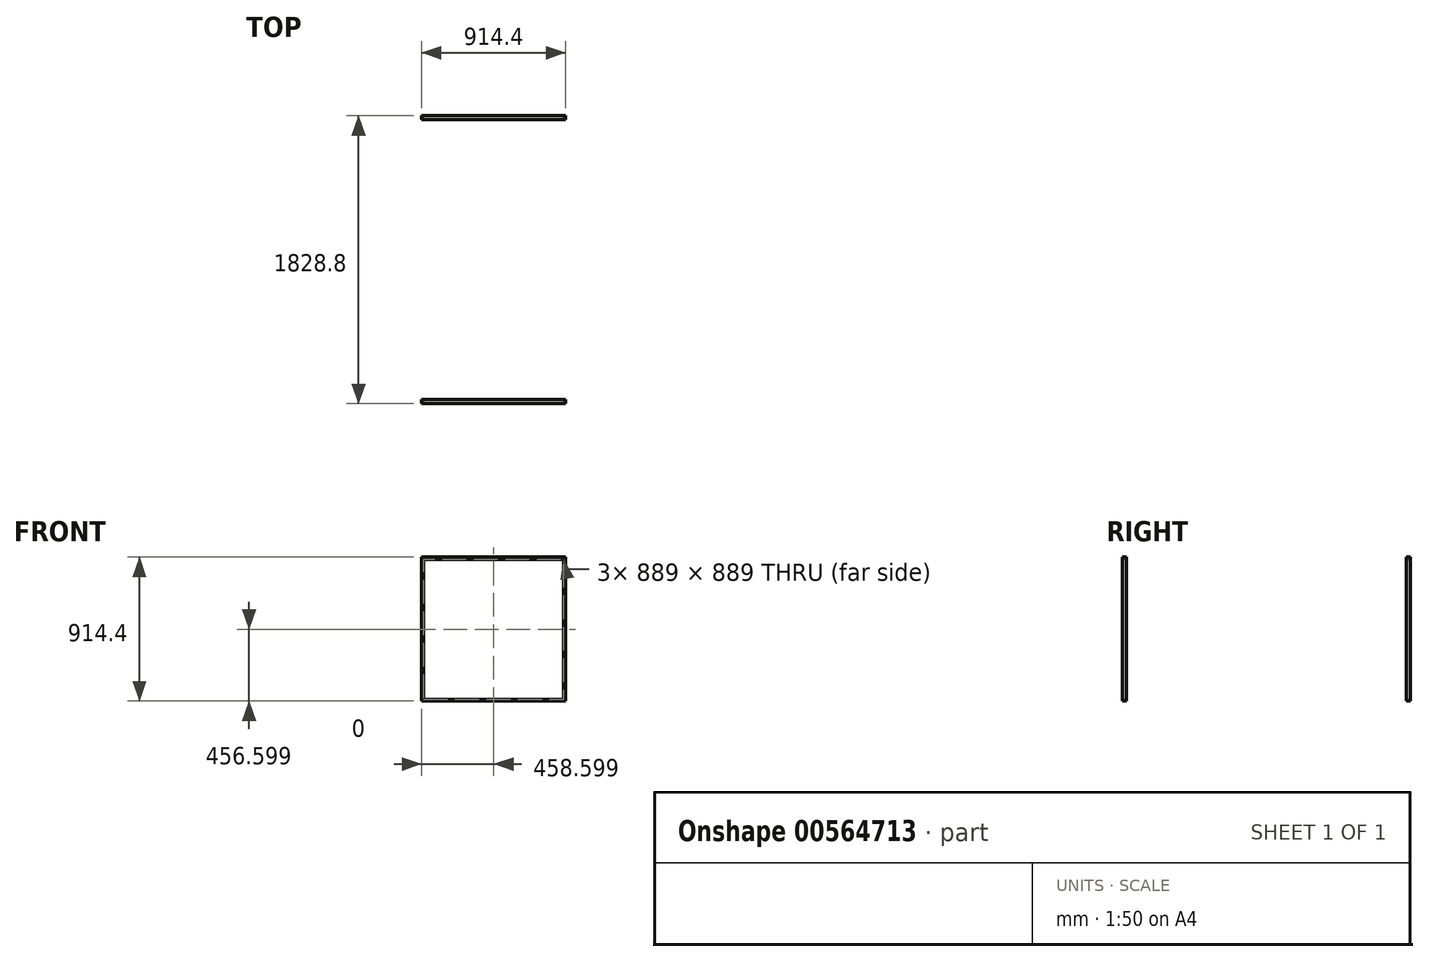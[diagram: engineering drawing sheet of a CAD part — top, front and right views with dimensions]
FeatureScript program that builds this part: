
annotation { "Feature Type Name" : "Feature", "Feature Type Description" : "" }
export const myFeature = defineFeature(function(context is Context, id is Id, definition is map)
    precondition{}
    {
        {
            var Q0;
            Q0=qCreatedBy(makeId("Front.planeOp"),FACE);
            var sketch = newSketch(context, id + "F0", { "sketchPlane" : qUnion([Q0])});
            skLineSegment(sketch, "E0.bottom", {"start": v(-523.13, 446.38) * mm, "end": v(391.27, 446.38) * mm});
            skLineSegment(sketch, "E0.top", {"start": v(-523.13, -468.02) * mm, "end": v(391.27, -468.02) * mm});
            skLineSegment(sketch, "E0.left", {"start": v(-523.13, 446.38) * mm, "end": v(-523.13, -468.02) * mm});
            skLineSegment(sketch, "E0.right", {"start": v(391.27, 446.38) * mm, "end": v(391.27, -468.02) * mm});
            skLineSegment(sketch, "E1.bottom", {"start": v(-509.03, 433.08) * mm, "end": v(379.97, 433.08) * mm});
            skLineSegment(sketch, "E1.top", {"start": v(-509.03, -455.92) * mm, "end": v(379.97, -455.92) * mm});
            skLineSegment(sketch, "E1.left", {"start": v(-509.03, 433.08) * mm, "end": v(-509.03, -455.92) * mm});
            skLineSegment(sketch, "E1.right", {"start": v(379.97, 433.08) * mm, "end": v(379.97, -455.92) * mm});
            skSolve(sketch);
        }
        {
            var Q0;
            Q0=makeQuery(id+"F0.imprint","IMPRINT",FACE,{"disambiguationData":[TD([[makeQuery(id+"F0.imprint","IMPRINT",EDGE,{"derivedFrom":sQuery(id+"F0.wireOp",EDGE,"E0.bottom")}),-1.0]])]});
            extrude(context, id + "F1", {"entities" : qUnion([Q0]), "depth" : 25.4 * mm, "offsetDistance" : 25.4 * mm});
        }
        {
            var Q0;
            Q0=qCreatedBy(makeId("Front.planeOp"),FACE);
            cPlane(context, id + "F2", {"entities" : qUnion([Q0]), "cplaneType" : CPlaneType.OFFSET, "offset" : 914.4 * mm, "width" : 152.4 * mm, "height" : 152.4 * mm});
        }
        {
            var Q0;
            Q0=makeQuery(id+"F1.opExtrude","SWEPT_BODY",BODY,{"disambiguationData":[OSD([sQuery(id+"F0.wireOp",EDGE,"E0.bottom"),sQuery(id+"F0.wireOp",EDGE,"E0.top"),sQuery(id+"F0.wireOp",EDGE,"E0.left"),sQuery(id+"F0.wireOp",EDGE,"E0.right"),sQuery(id+"F0.wireOp",EDGE,"E1.bottom"),sQuery(id+"F0.wireOp",EDGE,"E1.top"),sQuery(id+"F0.wireOp",EDGE,"E1.left"),sQuery(id+"F0.wireOp",EDGE,"E1.right")])]});
            transform(context, id + "F3", {"entities" : qUnion([Q0]), "transformType" : TransformType.COPY});
        }
        {
            var Q0;
            Q0=makeQuery(id+"F1.opExtrude","SWEPT_BODY",BODY,{"disambiguationData":[OSD([sQuery(id+"F0.wireOp",EDGE,"E0.bottom"),sQuery(id+"F0.wireOp",EDGE,"E0.top"),sQuery(id+"F0.wireOp",EDGE,"E0.left"),sQuery(id+"F0.wireOp",EDGE,"E0.right"),sQuery(id+"F0.wireOp",EDGE,"E1.bottom"),sQuery(id+"F0.wireOp",EDGE,"E1.top"),sQuery(id+"F0.wireOp",EDGE,"E1.left"),sQuery(id+"F0.wireOp",EDGE,"E1.right")])]});
            var Q1;
            Q1=qCreatedBy(id+"F2.planeOp",FACE);
            mirror(context, id + "F4", {"entities" : qUnion([Q0]), "mirrorPlane" : qUnion([Q1])});
        }
    });
